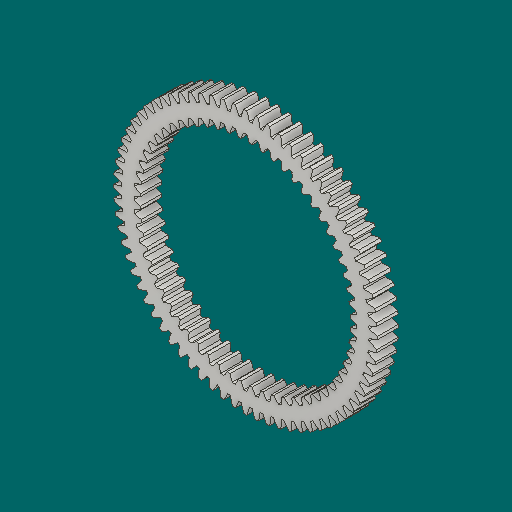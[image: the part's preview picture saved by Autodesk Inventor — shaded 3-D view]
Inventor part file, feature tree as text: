
AUTODESK INVENTOR PART (.ipt)
format: ipt  version: 2023.1 (Build 271208000, 208)  size: 908,288 bytes
history: native  units: in
note: dims shown in document units (in); Inventor stores cm internally (conversion verified against a paired STEP export)
features: other x13, sketch x3, plane x3
ambient origin geometry x8: Origin, YZ Plane, XZ Plane, XY Plane, X Axis, Y Axis, Z Axis, Center Point
bodies: Solid1_1 (feature_tree)
feature tree (19):
  other  "Spur Gear1"
  other  "Solid1::Spur Gear1"
  other  "Solid1_1::Spur Gear1"
  other  "TaggingFeature1"
  sketch  "Sketch1"  dims[d0=0.3937in]
  sketch  "Sketch2"  dims[d9=0.0in]
  sketch  "Sketch3"  dims[d14=0.0in d15=3.6in d16=0.0in d17=0.0in d18=0.0in d19=3.6in]
  plane  "XZ Plane_1"
  plane  "Work Plane2"
  plane  "Work Plane3"
  other  "Srf1"
  other  "Srf1::Derived"
  other  "Start plane iMate"
  other  "Distance iMate"
  other  "Position iMate"
  other  "Mesh iMate"
  other  "Axis iMate"
  other  "Mesh iMate2"
  other  "Align iMate"
